# Revit family: Door-Operator_Electric_Tormax_1201
name_source: partatom
category: Generic Models
units: mm (PartAtom-declared; Revit-internal decimal feet)

## family parameters
Always vertical = No
Can host rebar = No
Classification Number = 23.30.40.11.34
Cut with Voids When Loaded = No
Maintain Annotation Orientation = No
Part Type = Normal
Room Calculation Point = No
Round Connector Dimension = Use Diameter
Shared = No
Work Plane-Based = Yes

## types (1)
- as Specified
    Assembly Code = C1020410
    Available Options = as Specified
    Capacity = as Specified
    Construction Details = https://www.arcat.com
    Default Elevation = 4' - 0"
    Description = Tormax Product as Specified
    Expected Lifespan (Years) = 0
    Green Building-LEED = https://www.arcat.com
    Keynote = 08 71 13
    Maintenance Schedule (Months) = 0
    Manufacturer = TORMAX USA Inc.
    Manufacturer Fax = 210-494-5930
    Manufacturer Website = http://www.tormaxusa.com
    Model = as Specified
    Operator Arm Side A = Operator Arm : Standard Arm
    Operator Arm Side B = Operator Arm : Standard Arm
    Product Data = https://www.arcat.com
    Revision = R1_2018-04
    Sales Information = http://www.tormaxusa.com
    Sound Pressure = as Specified
    SpecWizard = https://www.arcat.com
    Specification = https://www.arcat.com
    Standards Conformance = as Specified
    URL = http://www.tormaxusa.com
    Unit Depth = 0' - 5"
    Unit Height = 0' - 4 9/16"
    Warranty Duration (Years) = 0
    Wind Load = as Specified

## geometry (parser evidence)
native form markers: Sweep x4
no freeform markers — native parametric forms only
